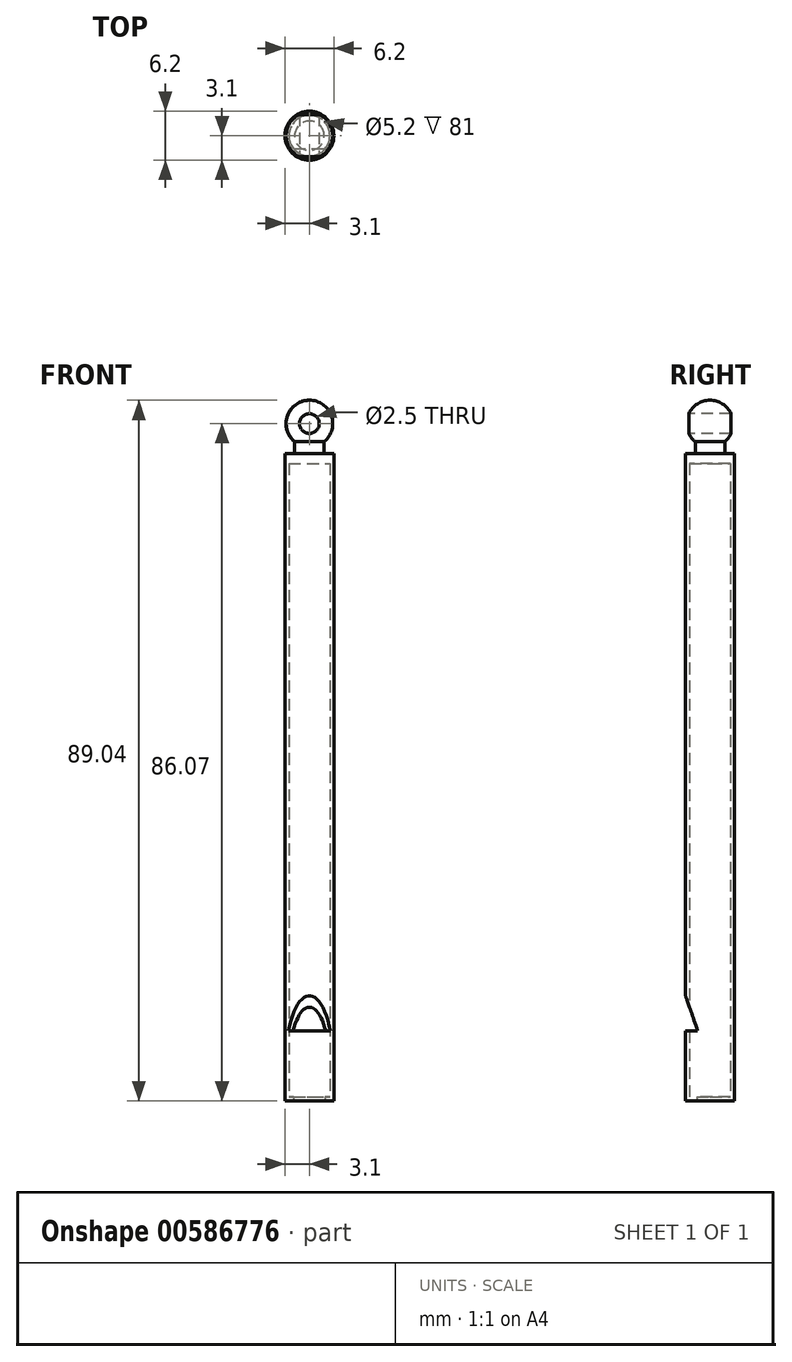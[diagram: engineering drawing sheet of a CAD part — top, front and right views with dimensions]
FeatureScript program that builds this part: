
annotation { "Feature Type Name" : "Feature", "Feature Type Description" : "" }
export const myFeature = defineFeature(function(context is Context, id is Id, definition is map)
    precondition{}
    {
        {
            var Q0;
            Q0=qCreatedBy(makeId("Front.planeOp"),FACE);
            var sketch = newSketch(context, id + "F0", { "sketchPlane" : qUnion([Q0])});
            skArc(sketch, "E0", {"start": v(0, 2.97) * mm, "mid": v(-2.8, 1) * mm, "end": v(-1.87, -2.3) * mm});
            skLineSegment(sketch, "E1", {"start": v(-1.87, -2.3) * mm, "end": v(-1.87, -3.8) * mm});
            skLineSegment(sketch, "E2", {"start": v(-1.87, -3.8) * mm, "end": v(-3.1, -3.8) * mm});
            skLineSegment(sketch, "E3", {"start": v(-3.1, -3.8) * mm, "end": v(-3.1, -86.07) * mm});
            skLineSegment(sketch, "E4", {"start": v(0, -86.07) * mm, "end": v(-3.1, -86.07) * mm});
            skLineSegment(sketch, "E5", {"start": v(0, -86.07) * mm, "end": v(0, 2.97) * mm});
            skPoint(sketch, "E6.end.orphan", {"position": v(1.88, -3.8) * mm});
            skSolve(sketch);
        }
        {
            var Q0;
            Q0=makeQuery(id+"F0.imprint","IMPRINT",FACE,{"disambiguationData":[TD([[makeQuery(id+"F0.imprint","IMPRINT",EDGE,{"derivedFrom":sQuery(id+"F0.wireOp",EDGE,"E0")}),1.0]])]});
            var Q1;
            Q1=sQuery(id+"F0.wireOp",EDGE,"E5");
            revolve(context, id + "F1", {"entities" : qUnion([Q0]), "axis" : qUnion([Q1]), "revolveType" : RevolveType.FULL});
        }
        {
            var Q0;
            Q0=qCreatedBy(makeId("Front.planeOp"),FACE);
            var sketch = newSketch(context, id + "F2", { "sketchPlane" : qUnion([Q0])});
            skCircle(sketch, "E7", {"center": v(0, 0) * mm, "radius": 1.25 * mm});
            skSolve(sketch);
        }
        {
            var Q0;
            Q0 = qSketchRegion(id + "F2", true);
            extrude(context, id + "F3", {"entities" : qUnion([Q0]), "operationType" : NewBodyOperationType.REMOVE, "endBound" : BoundingType.SYMMETRIC, "oppositeDirection" : true, "depth" : 25.4 * mm, "offsetDistance" : 25.4 * mm});
        }
        {
            var Q0;
            Q0=qCreatedBy(makeId("Right.planeOp"),FACE);
            var sketch = newSketch(context, id + "F4", { "sketchPlane" : qUnion([Q0])});
            skLineSegment(sketch, "E8", {"start": v(0, -86.07) * mm, "end": v(0, -77.17) * mm});
            skLineSegment(sketch, "E9", {"start": v(-3.1, -77.17) * mm, "end": v(-1.56, -77.17) * mm});
            skLineSegment(sketch, "E10", {"start": v(-3.1, -77.17) * mm, "end": v(-3.1, -72.67) * mm});
            skLineSegment(sketch, "E11", {"start": v(-3.1, -72.67) * mm, "end": v(-1.56, -77.17) * mm});
            skSolve(sketch);
        }
        {
            var Q0;
            Q0 = qSketchRegion(id + "F4", true);
            extrude(context, id + "F5", {"entities" : qUnion([Q0]), "operationType" : NewBodyOperationType.REMOVE, "endBound" : BoundingType.SYMMETRIC, "depth" : 25.4 * mm, "offsetDistance" : 25.4 * mm});
        }
        {
            var Q0;
            Q0=makeQuery(id+"F1.opRevolve","SWEPT_FACE",FACE,{"disambiguationData":[OSD([sQuery(id+"F0.wireOp",EDGE,"E4")])]});
            var sketch = newSketch(context, id + "F6", { "sketchPlane" : qUnion([Q0])});
            skCircle(sketch, "E12", {"center": v(0, 0) * mm, "radius": 2.6 * mm});
            skSolve(sketch);
        }
        {
            var Q0;
            Q0=makeQuery(id+"F6.imprint","IMPRINT",FACE,{"disambiguationData":[TD([[makeQuery(id+"F6.imprint","IMPRINT",EDGE,{"derivedFrom":sQuery(id+"F6.wireOp",EDGE,"E12")}),1.0]])]});
            extrude(context, id + "F7", {"entities" : qUnion([Q0]), "operationType" : NewBodyOperationType.REMOVE, "oppositeDirection" : true, "depth" : 81 * mm, "offsetDistance" : 25.4 * mm});
        }
        {
            var Q0;
            Q0=makeQuery(id+"F1.opRevolve","SWEPT_FACE",FACE,{"disambiguationData":[OSD([sQuery(id+"F0.wireOp",EDGE,"E4")])]});
            var sketch = newSketch(context, id + "F8", { "sketchPlane" : qUnion([Q0])});
            skCircle(sketch, "E13", {"center": v(0, 0) * mm, "radius": 2.6 * mm});
            skLineSegment(sketch, "E14", {"start": v(-2, 1.66) * mm, "end": v(2, 1.66) * mm});
            skSolve(sketch);
        }
        {
            var Q0;
            {var subQ0=sQuery(id+"F8.wireOp",EDGE,"E14");Q0=makeQuery(id+"F8.imprint","IMPRINT",FACE,{"disambiguationData":[TD([[makeQuery(id+"F8.imprint","IMPRINT",EDGE,{"derivedFrom":subQ0}),-1.0]])]});}
            extrude(context, id + "F9", {"entities" : qUnion([Q0]), "operationType" : NewBodyOperationType.ADD, "oppositeDirection" : true, "depth" : .5 * mm, "offsetDistance" : 25.4 * mm});
        }
    });
